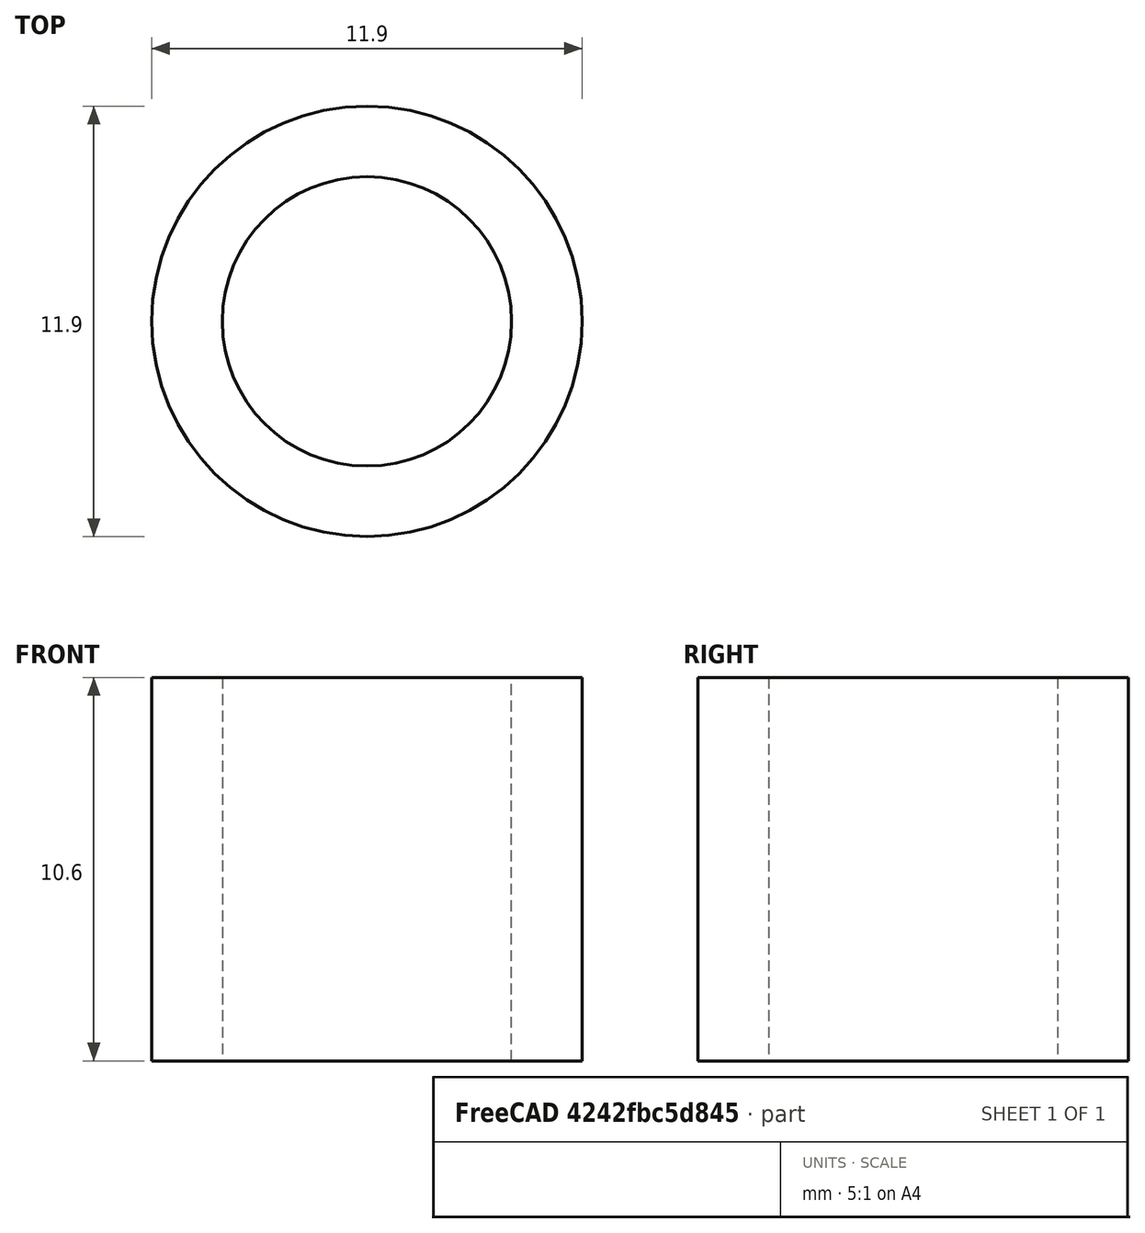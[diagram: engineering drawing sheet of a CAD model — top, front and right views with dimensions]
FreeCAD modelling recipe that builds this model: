
FCSTD DOCUMENT  (FreeCAD 0.21R33668 +26 (Git))
Label: cover_wheel_12-8v2
License: All rights reserved
LicenseURL: https://en.wikipedia.org/wiki/All_rights_reserved
objects: Sketcher::SketchObject×1, PartDesign::Pad×1, PartDesign::Body×1
note: 4 computed .brp shape members not serialized (recipe doc carries the construction recipe); baked Part::Feature solids carry a one-line shape summary decoded from their .brp

FEATURE [Sketcher::SketchObject] Sketch
  FullyConstrained = true
  MapMode = 5
  Support = -> [XY_Plane]
  sketch-geometry (2):
    g0: Circle CenterX=0 CenterY=0 CenterZ=0 NormalX=0 NormalY=0 NormalZ=1 AngleXU=0 Radius=5.95
    g1: Circle CenterX=0 CenterY=0 CenterZ=0 NormalX=0 NormalY=0 NormalZ=1 AngleXU=0 Radius=4
  constraints (4):
    c: Coincident(g0,g-1)
    c: Diameter(g0) = 11.9
    c: Coincident(g1,g0)
    c: Diameter(g1) = 8
FEATURE [PartDesign::Pad] Pad
  Direction = (0,0,1)
  Length = 10.6
  Length2 = 10
  Profile = -> Sketch
  ReferenceAxis = -> Sketch [N_Axis]
  Type = 0
FEATURE [PartDesign::Body] Body
  Group = -> [Sketch,Pad]
  Origin = -> Origin
  Tip = -> Pad
